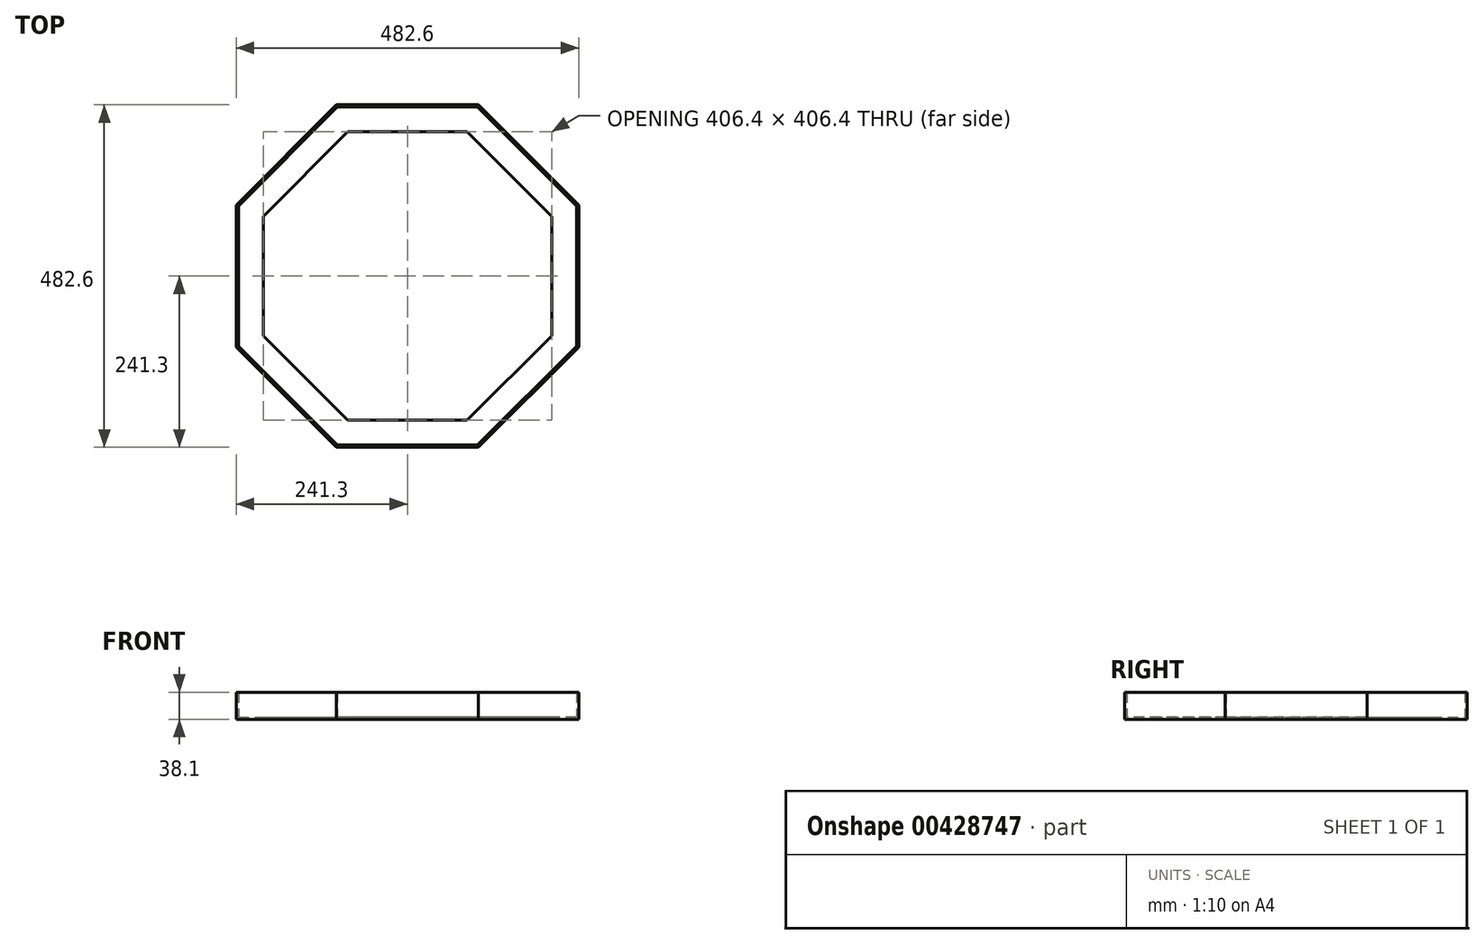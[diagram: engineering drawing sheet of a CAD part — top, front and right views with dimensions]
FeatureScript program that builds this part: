
annotation { "Feature Type Name" : "Feature", "Feature Type Description" : "" }
export const myFeature = defineFeature(function(context is Context, id is Id, definition is map)
    precondition{}
    {
        {
            var Q0;
            Q0=qCreatedBy(makeId("Front.planeOp"),FACE);
            var sketch = newSketch(context, id + "F0", { "sketchPlane" : qUnion([Q0])});
            skLineSegment(sketch, "E0", {"start": v(-241.3, 38.1) * mm, "end": v(-241.3, 0) * mm});
            skLineSegment(sketch, "E1", {"start": v(-241.3, 0) * mm, "end": v(-203.2, 0) * mm});
            skLineSegment(sketch, "E2", {"start": v(-203.2, 0) * mm, "end": v(-203.2, 3.17) * mm});
            skLineSegment(sketch, "E3", {"start": v(-203.2, 3.17) * mm, "end": v(-238.13, 3.17) * mm});
            skLineSegment(sketch, "E4", {"start": v(-238.12, 3.17) * mm, "end": v(-238.12, 38.1) * mm});
            skLineSegment(sketch, "E5", {"start": v(-238.12, 38.1) * mm, "end": v(-241.3, 38.1) * mm});
            skSolve(sketch);
        }
        {
            var Q0;
            Q0=qCreatedBy(makeId("Top.planeOp"),FACE);
            var sketch = newSketch(context, id + "F1", { "sketchPlane" : qUnion([Q0])});
            skLineSegment(sketch, "E6", {"start": v(-241.3, 0) * mm, "end": v(-241.3, 99.95) * mm});
            skLineSegment(sketch, "E7", {"start": v(-241.3, 99.95) * mm, "end": v(-99.95, 241.3) * mm});
            skLineSegment(sketch, "E8", {"start": v(-99.95, 241.3) * mm, "end": v(99.95, 241.3) * mm});
            skLineSegment(sketch, "E9", {"start": v(99.95, 241.3) * mm, "end": v(241.3, 99.95) * mm});
            skLineSegment(sketch, "E10", {"start": v(241.3, 99.95) * mm, "end": v(241.3, -99.95) * mm});
            skLineSegment(sketch, "E11", {"start": v(241.3, -99.95) * mm, "end": v(99.95, -241.3) * mm});
            skLineSegment(sketch, "E12", {"start": v(99.95, -241.3) * mm, "end": v(-99.95, -241.3) * mm});
            skLineSegment(sketch, "E13", {"start": v(-99.95, -241.3) * mm, "end": v(-241.3, -99.95) * mm});
            skLineSegment(sketch, "E14", {"start": v(-241.3, -99.95) * mm, "end": v(-241.3, 0) * mm});
            skSolve(sketch);
        }
        {
            var Q0;
            Q0 = qSketchRegion(id + "F0", true);
            var Q1;
            Q1 = qConstructionFilter(qBodyType(qCreatedBy(id + "F1" ,EDGE), BodyType.WIRE), ConstructionObject.NO);
            sweep(context, id + "F2", {"profiles" : qUnion([Q0]), "path" : qUnion([Q1])});
        }
    });
